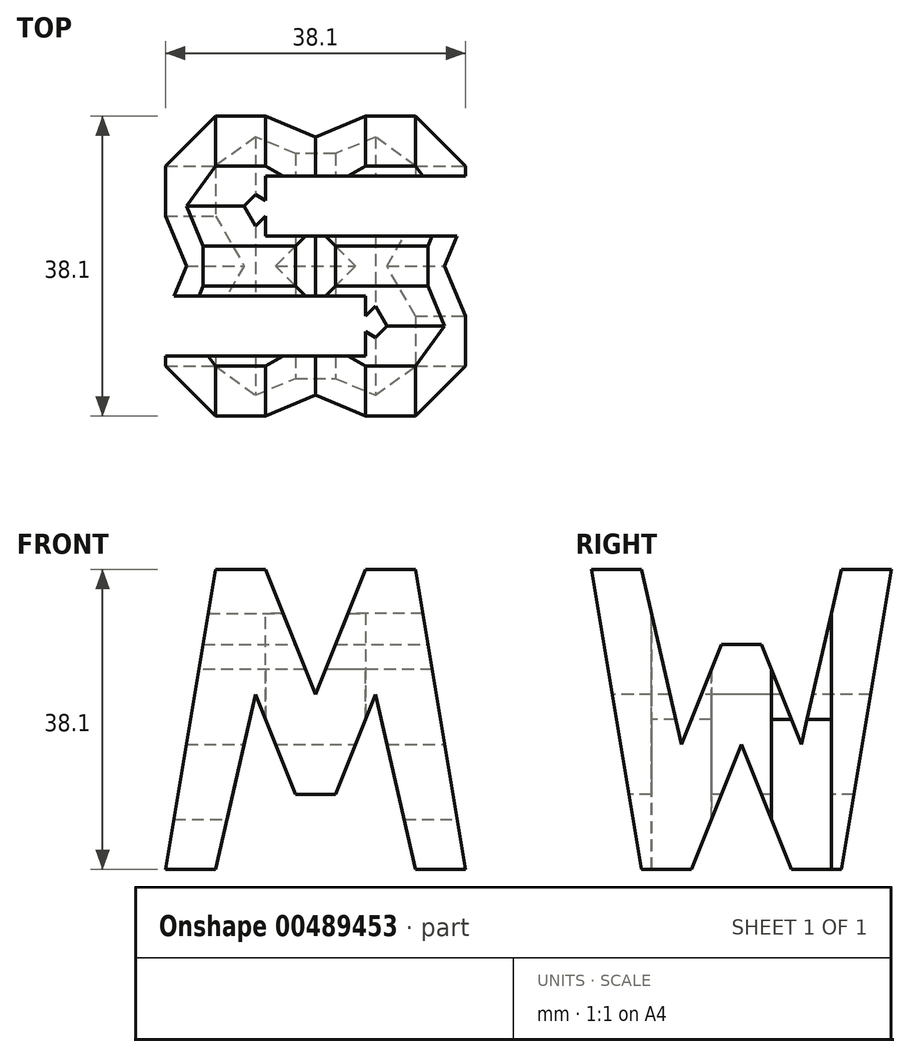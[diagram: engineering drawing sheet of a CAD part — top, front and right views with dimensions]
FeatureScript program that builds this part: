
annotation { "Feature Type Name" : "Feature", "Feature Type Description" : "" }
export const myFeature = defineFeature(function(context is Context, id is Id, definition is map)
    precondition{}
    {
        {
            var Q0;
            Q0=qCreatedBy(makeId("Front.planeOp"),FACE);
            var sketch = newSketch(context, id + "F0", { "sketchPlane" : qUnion([Q0])});
            skLineSegment(sketch, "E0", {"start": v(0, 0) * mm, "end": v(38.1, 0) * mm});
            skLineSegment(sketch, "E1", {"start": v(38.1, 0) * mm, "end": v(38.1, 38.1) * mm});
            skLineSegment(sketch, "E2", {"start": v(38.1, 38.1) * mm, "end": v(0, 38.1) * mm});
            skLineSegment(sketch, "E3", {"start": v(0, 38.1) * mm, "end": v(0, 0) * mm});
            skSolve(sketch);
        }
        {
            var Q0;
            Q0=makeQuery(id+"F0.imprint","IMPRINT",FACE,{"disambiguationData":[TD([[makeQuery(id+"F0.imprint","IMPRINT",EDGE,{"derivedFrom":sQuery(id+"F0.wireOp",EDGE,"E0")}),1.0]])]});
            extrude(context, id + "F1", {"entities" : qUnion([Q0]), "depth" : 38.1 * mm, "offsetDistance" : 25.4 * mm});
        }
        {
            var Q0;
            Q0=qCreatedBy(makeId("Front.planeOp"),FACE);
            cPlane(context, id + "F2", {"entities" : qUnion([Q0]), "cplaneType" : CPlaneType.OFFSET, "offset" : 38.1 * mm, "width" : 152.4 * mm, "height" : 152.4 * mm});
        }
        {
            var Q0;
            Q0=qCreatedBy(makeId("Right.planeOp"),FACE);
            cPlane(context, id + "F3", {"entities" : qUnion([Q0]), "cplaneType" : CPlaneType.OFFSET, "offset" : 38.1 * mm, "width" : 152.4 * mm, "height" : 152.4 * mm});
        }
        {
            var Q0;
            Q0=qCreatedBy(makeId("Top.planeOp"),FACE);
            cPlane(context, id + "F4", {"entities" : qUnion([Q0]), "cplaneType" : CPlaneType.OFFSET, "offset" : 38.1 * mm, "width" : 152.4 * mm, "height" : 152.4 * mm});
        }
        {
            var Q0;
            Q0=qCreatedBy(id+"F3.planeOp",FACE);
            var sketch = newSketch(context, id + "F5", { "sketchPlane" : qUnion([Q0])});
            skLineSegment(sketch, "E4", {"start": v(-38.1, 38.1) * mm, "end": v(-38.1, 0) * mm});
            skLineSegment(sketch, "E5", {"start": v(-38.1, 0) * mm, "end": v(0, 0) * mm});
            skLineSegment(sketch, "E6", {"start": v(0, 0) * mm, "end": v(0, 38.1) * mm});
            skLineSegment(sketch, "E7", {"start": v(0, 38.1) * mm, "end": v(-38.1, 38.1) * mm});
            skLineSegment(sketch, "E8", {"start": v(-38.1, 38.1) * mm, "end": v(-31.75, 0) * mm});
            skLineSegment(sketch, "E9", {"start": v(-31.75, 0) * mm, "end": v(-25.4, 0) * mm});
            skLineSegment(sketch, "E10", {"start": v(-25.4, 0) * mm, "end": v(-19.05, 15.88) * mm});
            skLineSegment(sketch, "E11", {"start": v(-19.05, 15.88) * mm, "end": v(-12.7, 0) * mm});
            skLineSegment(sketch, "E12", {"start": v(-12.7, 0) * mm, "end": v(-6.35, 0) * mm});
            skLineSegment(sketch, "E13", {"start": v(-6.35, 0) * mm, "end": v(0, 38.1) * mm});
            skLineSegment(sketch, "E14", {"start": v(-6.35, 38.1) * mm, "end": v(-11.43, 15.88) * mm});
            skLineSegment(sketch, "E15", {"start": v(-11.43, 15.88) * mm, "end": v(-16.5, 28.57) * mm});
            skLineSegment(sketch, "E16", {"start": v(-16.5, 28.57) * mm, "end": v(-21.59, 28.57) * mm});
            skLineSegment(sketch, "E17", {"start": v(-21.59, 28.57) * mm, "end": v(-26.67, 15.87) * mm});
            skLineSegment(sketch, "E18", {"start": v(-26.67, 15.88) * mm, "end": v(-31.75, 38.1) * mm});
            skSolve(sketch);
        }
        {
            var Q0;
            {var subQ0=sQuery(id+"F5.wireOp",EDGE,"E14");Q0=makeQuery(id+"F5.imprint","IMPRINT",FACE,{"disambiguationData":[TD([[makeQuery(id+"F5.imprint","IMPRINT",EDGE,{"derivedFrom":subQ0}),-1.0]])]});}
            var Q1;
            {var subQ0=sQuery(id+"F5.wireOp",EDGE,"E10");Q1=makeQuery(id+"F5.imprint","IMPRINT",FACE,{"disambiguationData":[TD([[makeQuery(id+"F5.imprint","IMPRINT",EDGE,{"derivedFrom":subQ0}),-1.0]])]});}
            var Q2;
            {var subQ0=sQuery(id+"F5.wireOp",EDGE,"E6");Q2=makeQuery(id+"F5.imprint","IMPRINT",FACE,{"disambiguationData":[TD([[makeQuery(id+"F5.imprint","IMPRINT",EDGE,{"derivedFrom":subQ0}),1.0]])]});}
            var Q3;
            {var subQ0=sQuery(id+"F5.wireOp",EDGE,"E4");Q3=makeQuery(id+"F5.imprint","IMPRINT",FACE,{"disambiguationData":[TD([[makeQuery(id+"F5.imprint","IMPRINT",EDGE,{"derivedFrom":subQ0}),1.0]])]});}
            extrude(context, id + "F6", {"entities" : qUnion([Q0, Q1, Q2, Q3]), "operationType" : NewBodyOperationType.REMOVE, "oppositeDirection" : true, "depth" : 38.1 * mm, "offsetDistance" : 25.4 * mm});
        }
        {
            var Q0;
            Q0=qCreatedBy(id+"F2.planeOp",FACE);
            var sketch = newSketch(context, id + "F7", { "sketchPlane" : qUnion([Q0])});
            skLineSegment(sketch, "E19", {"start": v(0, 0) * mm, "end": v(0, 38.1) * mm});
            skLineSegment(sketch, "E20", {"start": v(0, 38.1) * mm, "end": v(38.1, 38.1) * mm});
            skLineSegment(sketch, "E21", {"start": v(38.1, 38.1) * mm, "end": v(38.1, 0) * mm});
            skLineSegment(sketch, "E22", {"start": v(38.1, 0) * mm, "end": v(0, 0) * mm});
            skLineSegment(sketch, "E23", {"start": v(6.35, 38.1) * mm, "end": v(0, 0) * mm});
            skLineSegment(sketch, "E24", {"start": v(31.75, 38.1) * mm, "end": v(38.1, 0) * mm});
            skLineSegment(sketch, "E25", {"start": v(12.7, 38.1) * mm, "end": v(19.05, 22.23) * mm});
            skLineSegment(sketch, "E26", {"start": v(19.05, 22.22) * mm, "end": v(25.4, 38.1) * mm});
            skLineSegment(sketch, "E27", {"start": v(6.35, 0) * mm, "end": v(11.43, 22.23) * mm});
            skLineSegment(sketch, "E28", {"start": v(11.43, 22.22) * mm, "end": v(16.51, 9.52) * mm});
            skLineSegment(sketch, "E29", {"start": v(16.51, 9.53) * mm, "end": v(21.6, 9.53) * mm});
            skLineSegment(sketch, "E30", {"start": v(21.6, 9.52) * mm, "end": v(26.67, 22.23) * mm});
            skLineSegment(sketch, "E31", {"start": v(26.67, 22.23) * mm, "end": v(31.75, 0) * mm});
            skSolve(sketch);
        }
        {
            var Q0;
            {var subQ0=sQuery(id+"F7.wireOp",EDGE,"E19");Q0=makeQuery(id+"F7.imprint","IMPRINT",FACE,{"disambiguationData":[TD([[makeQuery(id+"F7.imprint","IMPRINT",EDGE,{"derivedFrom":subQ0}),-1.0]])]});}
            var Q1;
            {var subQ0=sQuery(id+"F7.wireOp",EDGE,"E25");Q1=makeQuery(id+"F7.imprint","IMPRINT",FACE,{"disambiguationData":[TD([[makeQuery(id+"F7.imprint","IMPRINT",EDGE,{"derivedFrom":subQ0}),1.0]])]});}
            var Q2;
            {var subQ0=sQuery(id+"F7.wireOp",EDGE,"E27");Q2=makeQuery(id+"F7.imprint","IMPRINT",FACE,{"disambiguationData":[TD([[makeQuery(id+"F7.imprint","IMPRINT",EDGE,{"derivedFrom":subQ0}),-1.0]])]});}
            var Q3;
            {var subQ0=sQuery(id+"F7.wireOp",EDGE,"E21");Q3=makeQuery(id+"F7.imprint","IMPRINT",FACE,{"disambiguationData":[TD([[makeQuery(id+"F7.imprint","IMPRINT",EDGE,{"derivedFrom":subQ0}),-1.0]])]});}
            extrude(context, id + "F8", {"entities" : qUnion([Q0, Q1, Q2, Q3]), "operationType" : NewBodyOperationType.REMOVE, "oppositeDirection" : true, "depth" : 38.1 * mm, "offsetDistance" : 25.4 * mm});
        }
        {
            var Q0;
            Q0=qCreatedBy(id+"F4.planeOp",FACE);
            var sketch = newSketch(context, id + "F9", { "sketchPlane" : qUnion([Q0])});
            skLineSegment(sketch, "E32", {"start": v(0, 0) * mm, "end": v(0, -38.1) * mm});
            skLineSegment(sketch, "E33", {"start": v(0, -38.1) * mm, "end": v(38.1, -38.1) * mm});
            skLineSegment(sketch, "E34", {"start": v(38.1, -38.1) * mm, "end": v(38.1, 0) * mm});
            skLineSegment(sketch, "E35", {"start": v(38.1, 0) * mm, "end": v(0, 0) * mm});
            skLineSegment(sketch, "E36", {"start": v(38.1, -7.62) * mm, "end": v(12.7, -7.62) * mm});
            skLineSegment(sketch, "E37", {"start": v(38.1, -15.24) * mm, "end": v(12.7, -15.24) * mm});
            skLineSegment(sketch, "E38", {"start": v(12.7, -15.24) * mm, "end": v(12.7, -7.62) * mm});
            skLineSegment(sketch, "E39", {"start": v(0, -30.48) * mm, "end": v(25.4, -30.48) * mm});
            skLineSegment(sketch, "E40", {"start": v(25.4, -30.48) * mm, "end": v(25.4, -22.86) * mm});
            skLineSegment(sketch, "E41", {"start": v(25.4, -22.86) * mm, "end": v(0, -22.86) * mm});
            skSolve(sketch);
        }
        {
            var Q0;
            {var subQ0=sQuery(id+"F9.wireOp",EDGE,"E36");Q0=makeQuery(id+"F9.imprint","IMPRINT",FACE,{"disambiguationData":[TD([[makeQuery(id+"F9.imprint","IMPRINT",EDGE,{"derivedFrom":subQ0}),1.0]])]});}
            var Q1;
            {var subQ0=sQuery(id+"F9.wireOp",EDGE,"E39");Q1=makeQuery(id+"F9.imprint","IMPRINT",FACE,{"disambiguationData":[TD([[makeQuery(id+"F9.imprint","IMPRINT",EDGE,{"derivedFrom":subQ0}),1.0]])]});}
            extrude(context, id + "F10", {"entities" : qUnion([Q0, Q1]), "operationType" : NewBodyOperationType.REMOVE, "oppositeDirection" : true, "depth" : 38.1 * mm, "offsetDistance" : 25.4 * mm});
        }
    });
